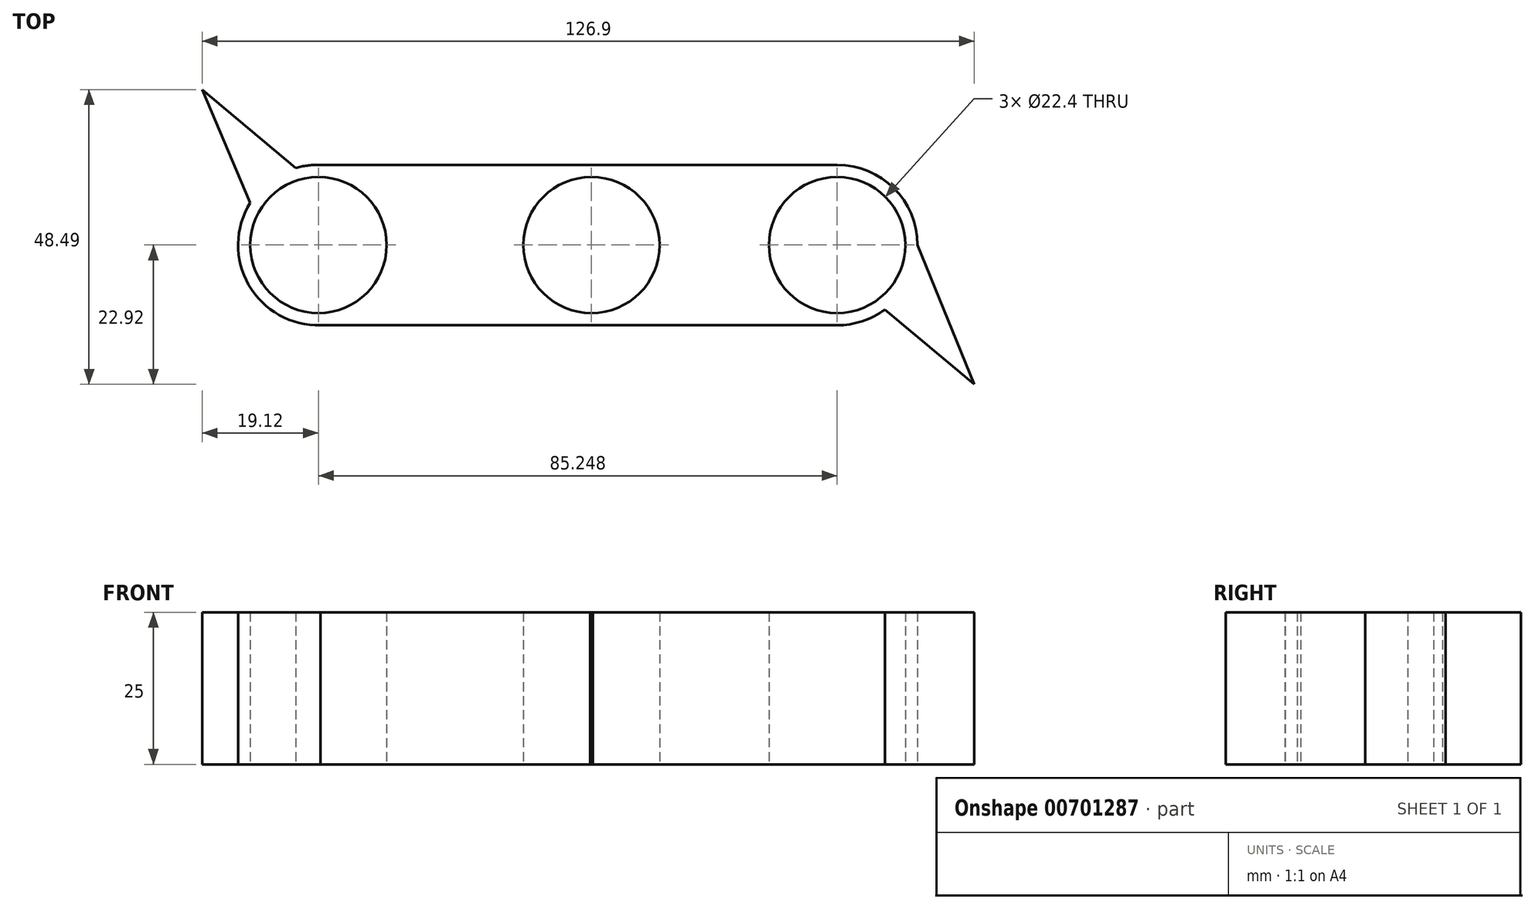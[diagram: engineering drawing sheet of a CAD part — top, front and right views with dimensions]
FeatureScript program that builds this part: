
annotation { "Feature Type Name" : "Feature", "Feature Type Description" : "" }
export const myFeature = defineFeature(function(context is Context, id is Id, definition is map)
    precondition{}
    {
        {
            var Q0;
            Q0=qCreatedBy(makeId("Top.planeOp"),FACE);
            var sketch = newSketch(context, id + "F0", { "sketchPlane" : qUnion([Q0])});
            skCircle(sketch, "E0", {"center": v(0, 0) * mm, "radius": 11.2 * mm});
            skCircle(sketch, "E1", {"center": v(0, 0) * mm, "radius": 13.2 * mm});
            skCircle(sketch, "E2", {"center": v(40.38, 0) * mm, "radius": 11.2 * mm});
            skCircle(sketch, "E3", {"center": v(40.38, 0) * mm, "radius": 13.2 * mm});
            skCircle(sketch, "E4", {"center": v(-44.87, 0) * mm, "radius": 11.2 * mm});
            skCircle(sketch, "E5", {"center": v(-44.87, 0) * mm, "radius": 13.2 * mm});
            skLineSegment(sketch, "E6", {"start": v(-44.8, 13.2) * mm, "end": v(40.38, 13.2) * mm});
            skLineSegment(sketch, "E7", {"start": v(-45.2, -13.2) * mm, "end": v(40.38, -13.2) * mm});
            skLineSegment(sketch, "E8", {"start": v(-56.1, 6.94) * mm, "end": v(-63.99, 25.57) * mm});
            skLineSegment(sketch, "E9", {"start": v(-63.99, 25.57) * mm, "end": v(-48.6, 12.66) * mm});
            skLineSegment(sketch, "E10", {"start": v(48.22, -10.62) * mm, "end": v(62.9, -22.92) * mm});
            skLineSegment(sketch, "E11", {"start": v(53.58, 0) * mm, "end": v(62.9, -22.92) * mm});
            skSolve(sketch);
        }
        {
            var Q0;
            Q0 = qSketchRegion(id + "F0", true);
            extrude(context, id + "F1", {"entities" : qUnion([Q0]), "depth" : 25 * mm, "offsetDistance" : 25 * mm});
        }
    });
